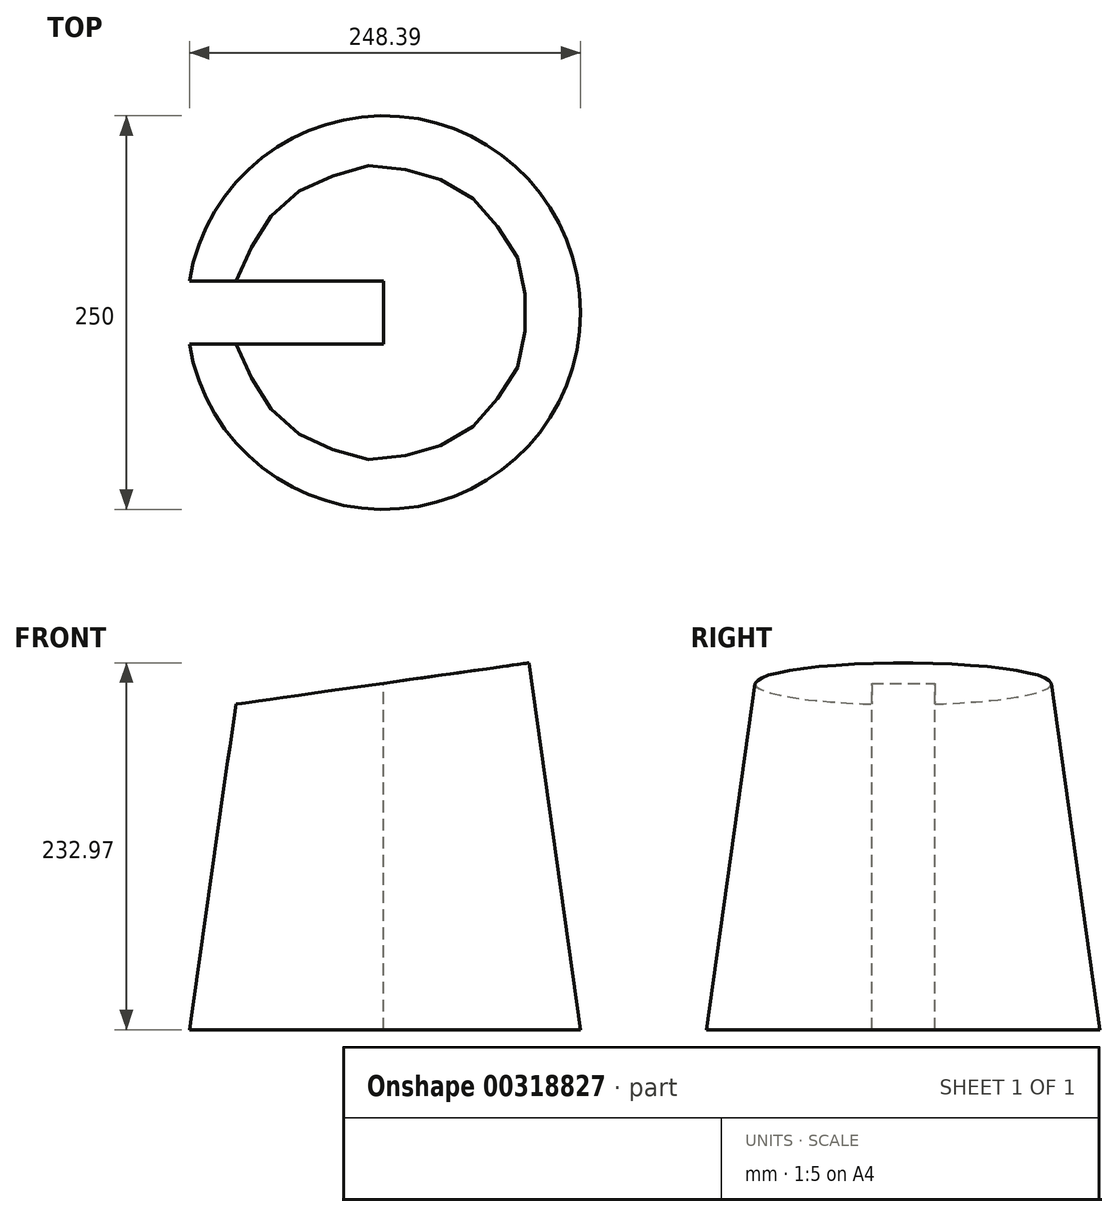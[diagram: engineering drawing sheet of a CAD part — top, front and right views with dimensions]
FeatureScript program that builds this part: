
annotation { "Feature Type Name" : "Feature", "Feature Type Description" : "" }
export const myFeature = defineFeature(function(context is Context, id is Id, definition is map)
    precondition{}
    {
        {
            var Q0;
            Q0=qCreatedBy(makeId("Top.planeOp"),FACE);
            var sketch = newSketch(context, id + "F0", { "sketchPlane" : qUnion([Q0])});
            skCircle(sketch, "E0", {"center": v(0, 0) * mm, "radius": 125 * mm});
            skSolve(sketch);
        }
        {
            var Q0;
            Q0=makeQuery(id+"F0.imprint","IMPRINT",FACE,{"disambiguationData":[TD([[makeQuery(id+"F0.imprint","IMPRINT",EDGE,{"derivedFrom":sQuery(id+"F0.wireOp",EDGE,"E0")}),1.0]])]});
            extrude(context, id + "F1", {"entities" : qUnion([Q0]), "depth" : 250 * mm, "offsetDistance" : 25 * mm, "hasDraft" : true, "draftAngle" : 8 * degree, "draftPullDirection" : true});
        }
        {
            var Q0;
            Q0=qCreatedBy(makeId("Right.planeOp"),FACE);
            var sketch = newSketch(context, id + "F2", { "sketchPlane" : qUnion([Q0])});
            skLineSegment(sketch, "E1.bottom", {"start": v(20, 0) * mm, "end": v(-20, 0) * mm});
            skLineSegment(sketch, "E1.top", {"start": v(20, 250) * mm, "end": v(-20, 250) * mm});
            skLineSegment(sketch, "E1.left", {"start": v(20, 0) * mm, "end": v(20, 250) * mm});
            skLineSegment(sketch, "E1.right", {"start": v(-20, 0) * mm, "end": v(-20, 250) * mm});
            skSolve(sketch);
        }
        {
            var Q0;
            Q0 = qSketchRegion(id + "F2", true);
            extrude(context, id + "F3", {"entities" : qUnion([Q0]), "operationType" : NewBodyOperationType.REMOVE, "oppositeDirection" : true, "depth" : 150 * mm, "offsetDistance" : 25 * mm});
        }
        {
            var Q0;
            Q0=qCreatedBy(makeId("Top.planeOp"),FACE);
            cPlane(context, id + "F4", {"entities" : qUnion([Q0]), "cplaneType" : CPlaneType.OFFSET, "offset" : 220 * mm, "width" : 150 * mm, "height" : 150 * mm});
        }
        {
            var Q0;
            Q0=qCreatedBy(id+"F4.planeOp",FACE);
            var sketch = newSketch(context, id + "F5", { "sketchPlane" : qUnion([Q0])});
            skLineSegment(sketch, "E2", {"start": v(0, 69.6) * mm, "end": v(0, -78.89) * mm, "construction": true});
            skSolve(sketch);
        }
        {
            var Q0;
            Q0=sQuery(id+"F5.wireOp",EDGE,"E2");
            cPlane(context, id + "F6", {"entities" : qUnion([Q0]), "cplaneType" : CPlaneType.LINE_ANGLE, "offset" : 25 * mm, "angle" : 8 * degree, "width" : 150 * mm, "height" : 150 * mm});
        }
        {
            var Q0;
            Q0=qCreatedBy(id+"F6.planeOp",FACE);
            var sketch = newSketch(context, id + "F7", { "sketchPlane" : qUnion([Q0])});
            skCircle(sketch, "E3", {"center": v(0, 0) * mm, "radius": 150 * mm});
            skSolve(sketch);
        }
        {
            var Q0;
            Q0 = qSketchRegion(id + "F7", true);
            extrude(context, id + "F8", {"entities" : qUnion([Q0]), "operationType" : NewBodyOperationType.REMOVE, "endBound" : BoundingType.THROUGH_ALL, "oppositeDirection" : true, "depth" : 25 * mm, "offsetDistance" : 25 * mm});
        }
    });
